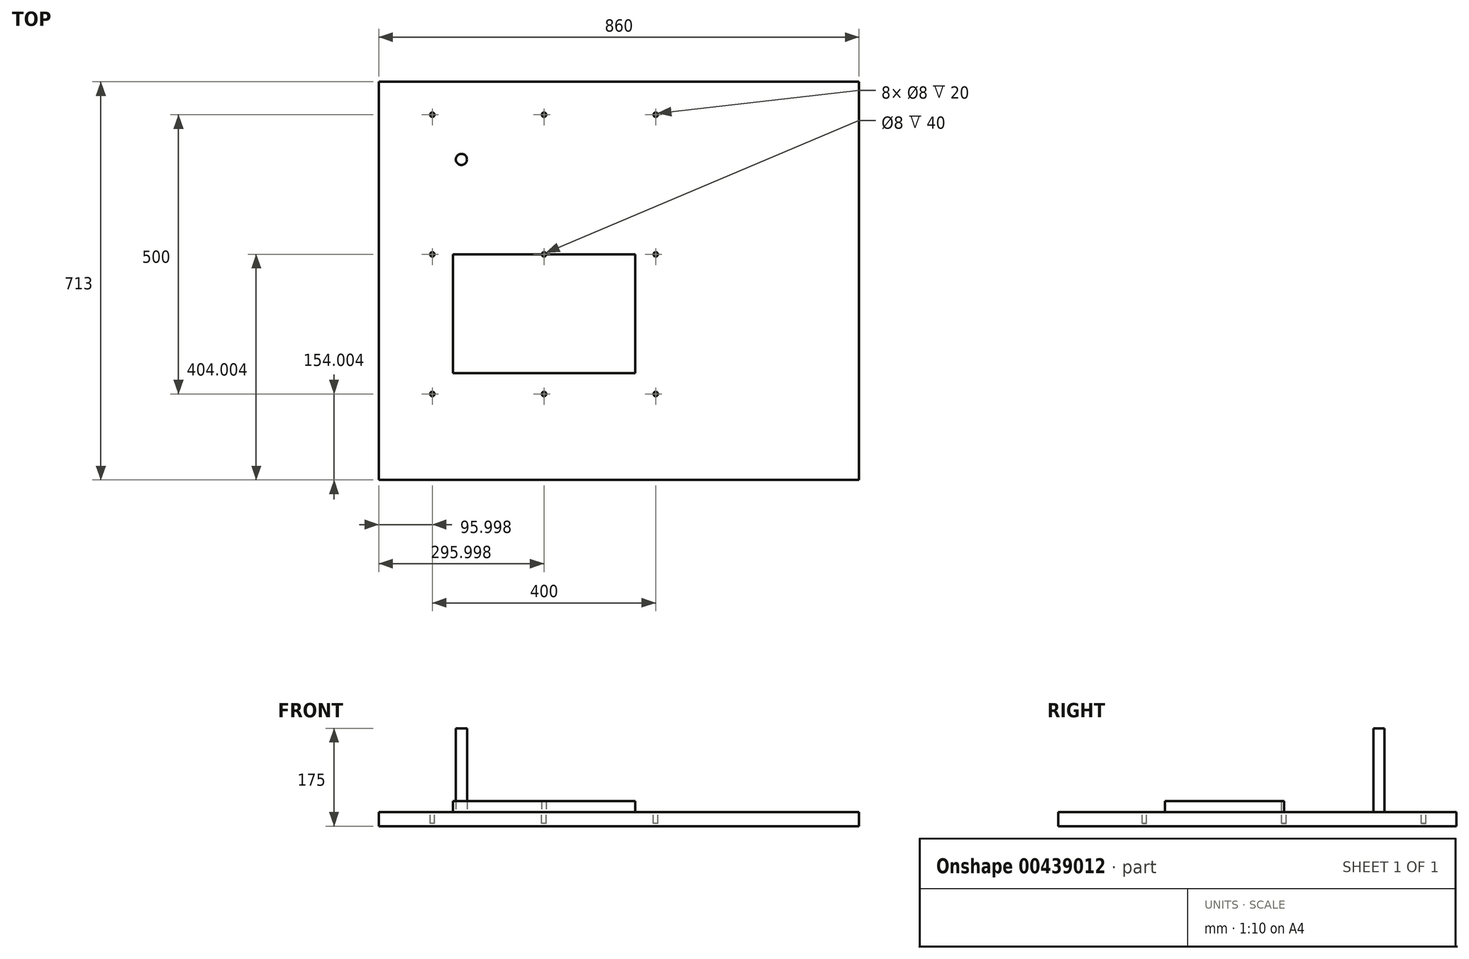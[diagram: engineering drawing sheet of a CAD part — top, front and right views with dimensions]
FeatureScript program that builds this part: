
annotation { "Feature Type Name" : "Feature", "Feature Type Description" : "" }
export const myFeature = defineFeature(function(context is Context, id is Id, definition is map)
    precondition{}
    {
        {
            var Q0;
            Q0=qCreatedBy(makeId("Top.planeOp"),FACE);
            var sketch = newSketch(context, id + "F0", { "sketchPlane" : qUnion([Q0])});
            skLineSegment(sketch, "E0.bottom", {"start": v(-802.36, 672.16) * mm, "end": v(57.64, 672.16) * mm});
            skLineSegment(sketch, "E0.top", {"start": v(-802.36, -40.84) * mm, "end": v(57.64, -40.84) * mm});
            skLineSegment(sketch, "E0.left", {"start": v(-802.36, 672.16) * mm, "end": v(-802.36, -40.84) * mm});
            skLineSegment(sketch, "E0.right", {"start": v(57.64, 672.16) * mm, "end": v(57.64, -40.84) * mm});
            skSolve(sketch);
        }
        {
            var Q0;
            Q0=makeQuery(id+"F0.imprint","IMPRINT",FACE,{"disambiguationData":[TD([[makeQuery(id+"F0.imprint","IMPRINT",EDGE,{"derivedFrom":sQuery(id+"F0.wireOp",EDGE,"E0.bottom")}),-1.0]])]});
            extrude(context, id + "F1", {"entities" : qUnion([Q0]), "oppositeDirection" : true, "depth" : 25 * mm});
        }
        {
            var Q0;
            Q0=makeQuery(id+"F1.opExtrude","CAP_FACE",FACE,{"disambiguationData":[OSD([sQuery(id+"F0.wireOp",EDGE,"E0.bottom"),sQuery(id+"F0.wireOp",EDGE,"E0.top"),sQuery(id+"F0.wireOp",EDGE,"E0.left"),sQuery(id+"F0.wireOp",EDGE,"E0.right")])],"isStart":true});
            var sketch = newSketch(context, id + "F2", { "sketchPlane" : qUnion([Q0])});
            skCircle(sketch, "E1", {"center": v(-706.36, 613.16) * mm, "radius": 4 * mm});
            skCircle(sketch, "E2", {"center": v(-506.36, 613.16) * mm, "radius": 4 * mm});
            skCircle(sketch, "E3", {"center": v(-306.36, 613.16) * mm, "radius": 4 * mm});
            skCircle(sketch, "E4", {"center": v(-706.36, 363.16) * mm, "radius": 4 * mm});
            skCircle(sketch, "E5", {"center": v(-506.36, 363.16) * mm, "radius": 4 * mm});
            skCircle(sketch, "E6", {"center": v(-306.36, 363.16) * mm, "radius": 4 * mm});
            skCircle(sketch, "E7", {"center": v(-706.36, 113.16) * mm, "radius": 4 * mm});
            skCircle(sketch, "E8", {"center": v(-506.36, 113.16) * mm, "radius": 4 * mm});
            skCircle(sketch, "E9", {"center": v(-306.36, 113.16) * mm, "radius": 4 * mm});
            skSolve(sketch);
        }
        {
            var Q0;
            Q0 = qSketchRegion(id + "F2", true);
            extrude(context, id + "F3", {"entities" : qUnion([Q0]), "operationType" : NewBodyOperationType.REMOVE, "oppositeDirection" : true, "depth" : 20 * mm});
        }
        {
            var Q0;
            Q0=makeQuery(id+"F1.opExtrude","CAP_FACE",FACE,{"disambiguationData":[OSD([sQuery(id+"F0.wireOp",EDGE,"E0.bottom"),sQuery(id+"F0.wireOp",EDGE,"E0.top"),sQuery(id+"F0.wireOp",EDGE,"E0.left"),sQuery(id+"F0.wireOp",EDGE,"E0.right")])],"isStart":true});
            var sketch = newSketch(context, id + "F4", { "sketchPlane" : qUnion([Q0])});
            skLineSegment(sketch, "E10.bottom", {"start": v(-669.36, 150.16) * mm, "end": v(-343.27, 150.16) * mm});
            skLineSegment(sketch, "E10.top", {"start": v(-669.36, 363.16) * mm, "end": v(-343.27, 363.16) * mm});
            skLineSegment(sketch, "E10.left", {"start": v(-669.36, 150.16) * mm, "end": v(-669.36, 363.16) * mm});
            skLineSegment(sketch, "E10.right", {"start": v(-343.27, 150.16) * mm, "end": v(-343.27, 363.16) * mm});
            skSolve(sketch);
        }
        {
            var Q0;
            Q0=makeQuery(id+"F4.imprint","IMPRINT",FACE,{"disambiguationData":[TD([[makeQuery(id+"F4.imprint","IMPRINT",EDGE,{"derivedFrom":sQuery(id+"F4.wireOp",EDGE,"E10.bottom")}),1.0]])]});
            extrude(context, id + "F5", {"entities" : qUnion([Q0]), "operationType" : NewBodyOperationType.ADD, "depth" : 20 * mm});
        }
        {
            var Q0;
            Q0=makeQuery(id+"F1.opExtrude","CAP_FACE",FACE,{"disambiguationData":[OSD([sQuery(id+"F0.wireOp",EDGE,"E0.bottom"),sQuery(id+"F0.wireOp",EDGE,"E0.top"),sQuery(id+"F0.wireOp",EDGE,"E0.left"),sQuery(id+"F0.wireOp",EDGE,"E0.right")])],"isStart":true});
            var sketch = newSketch(context, id + "F6", { "sketchPlane" : qUnion([Q0])});
            skCircle(sketch, "E11", {"center": v(-654.36, 533.16) * mm, "radius": 10 * mm});
            skSolve(sketch);
        }
        {
            var Q0;
            Q0=makeQuery(id+"F6.imprint","IMPRINT",FACE,{"disambiguationData":[TD([[makeQuery(id+"F6.imprint","IMPRINT",EDGE,{"derivedFrom":sQuery(id+"F6.wireOp",EDGE,"E11")}),1.0]])]});
            extrude(context, id + "F7", {"entities" : qUnion([Q0]), "operationType" : NewBodyOperationType.ADD, "depth" : 150 * mm});
        }
    });
